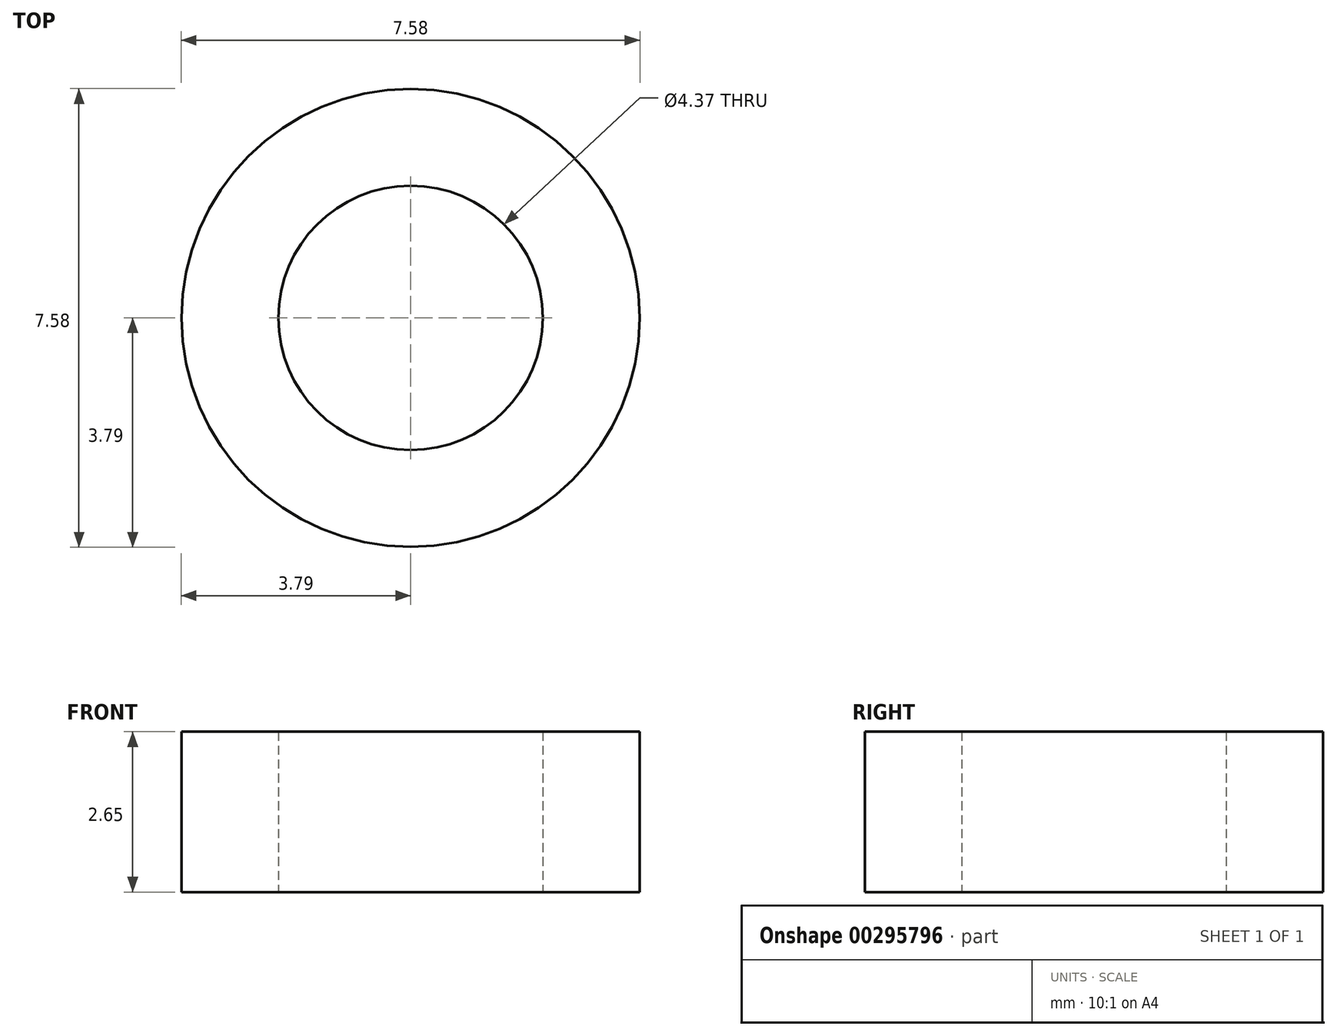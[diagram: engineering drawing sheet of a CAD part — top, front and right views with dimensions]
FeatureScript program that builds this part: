
annotation { "Feature Type Name" : "Feature", "Feature Type Description" : "" }
export const myFeature = defineFeature(function(context is Context, id is Id, definition is map)
    precondition{}
    {
        {
            assignVariable(context, id + "F0", {"name" : "spacerheight", "anyValue" : 2.48});
        }
        {
            var Q0;
            Q0=qCreatedBy(makeId("Top.planeOp"),FACE);
            var sketch = newSketch(context, id + "F1", { "sketchPlane" : qUnion([Q0])});
            skCircle(sketch, "E0", {"center": v(0, 0) * mm, "radius": 3.78 * mm});
            skCircle(sketch, "E1", {"center": v(0, 0) * mm, "radius": 2.19 * mm});
            skSolve(sketch);
        }
        {
            var Q0;
            Q0 = qSketchRegion(id + "F1", true);
            extrude(context, id + "F2", {"entities" : qUnion([Q0]), "depth" : (getVariable(context, 'spacerheight') + .17) * mm});
        }
    });
